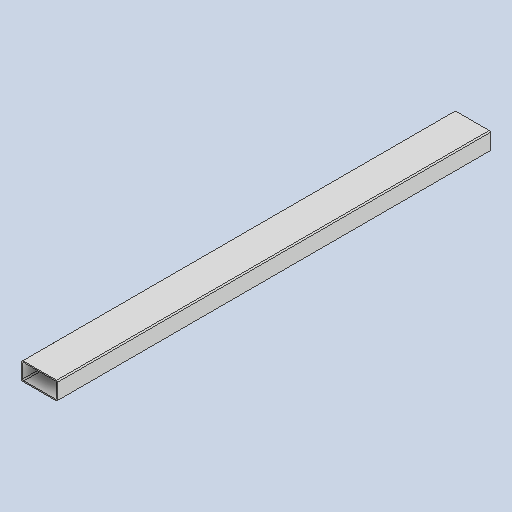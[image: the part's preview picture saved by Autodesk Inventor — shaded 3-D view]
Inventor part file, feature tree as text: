
AUTODESK INVENTOR PART (.ipt)
format: ipt  version: 2023 (Build 270158000, 158)  size: 173,056 bytes
history: native  units: in
note: dims shown in document units (in); Inventor stores cm internally (conversion verified against a paired STEP export)
features: extrude x1, shell x1, fillet x1, sketch x1
ambient origin geometry x8: Origin, YZ Plane, XZ Plane, XY Plane, X Axis, Y Axis, Z Axis, Center Point
bodies: Solid1 (feature_tree)
feature tree (4):
  extrude  "Extrusion1"  Depth=2.0in
  shell  "Shell1"  Thickness=48.0in
  fillet  "Fillet1"  Radius=0.125in
  sketch  "Sketch1"  dims[d0=4.0in d1=2.0in d2=48.0in d3=0.0in d4=0.125in d5=0.125in]
